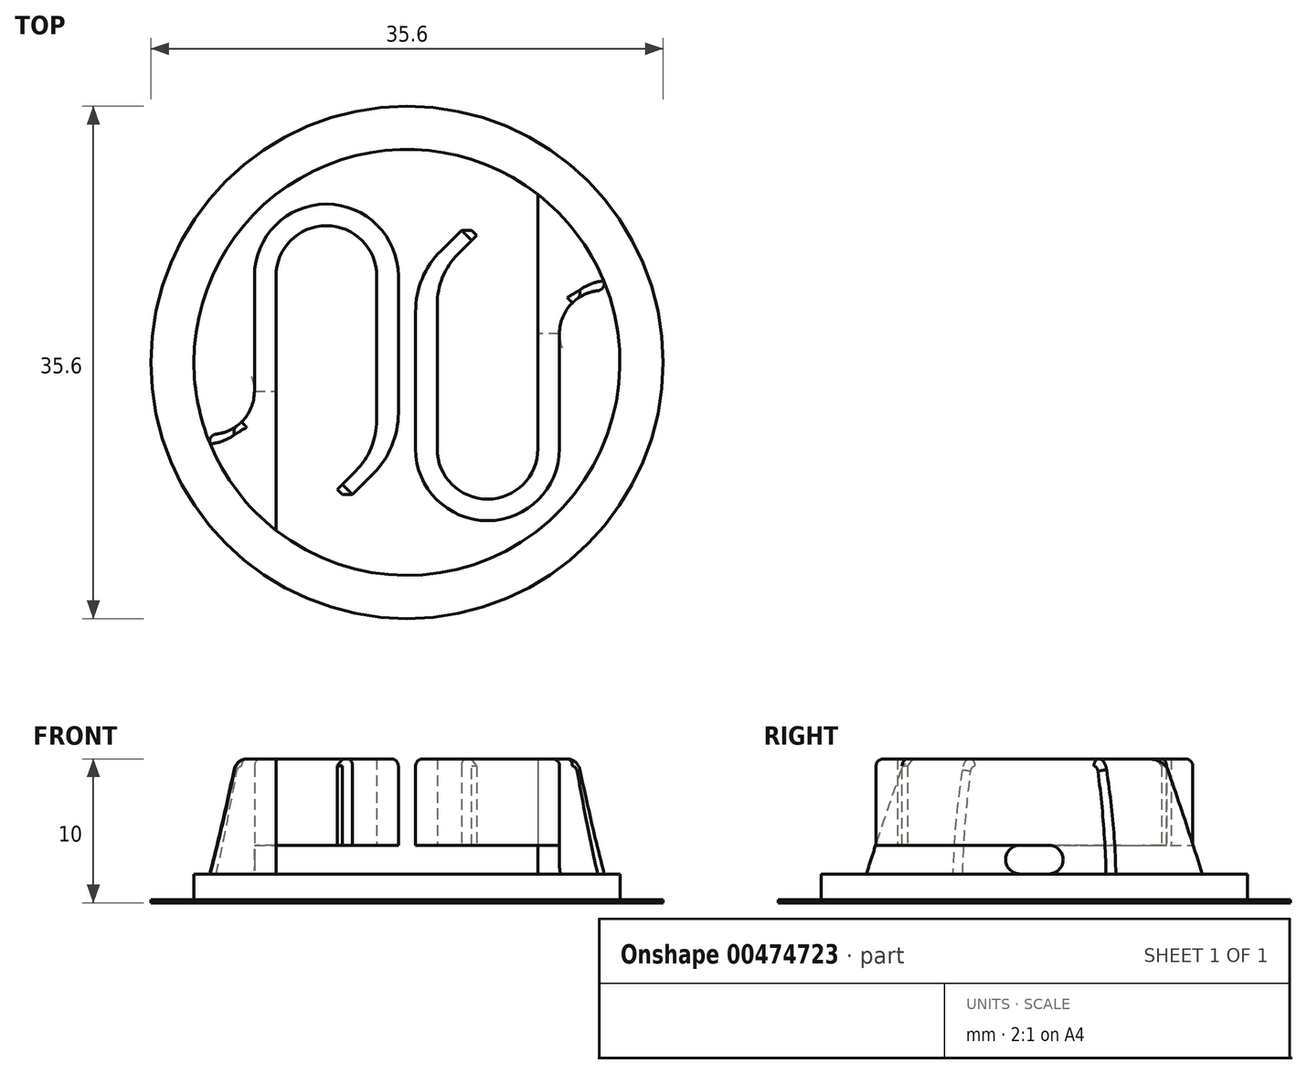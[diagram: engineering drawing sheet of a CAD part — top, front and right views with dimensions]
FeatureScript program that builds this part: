
annotation { "Feature Type Name" : "Feature", "Feature Type Description" : "" }
export const myFeature = defineFeature(function(context is Context, id is Id, definition is map)
    precondition{}
    {
        {
            var Q0;
            Q0=qCreatedBy(makeId("Top.planeOp"),FACE);
            var sketch = newSketch(context, id + "F0", { "sketchPlane" : qUnion([Q0])});
            skCircle(sketch, "E0", {"center": v(0, 0) * mm, "radius": 14.8 * mm});
            skSolve(sketch);
        }
        {
            var Q0;
            Q0=qSketchRegion(id+"F0",true);
            extrude(context, id + "F1", {"entities" : qUnion([Q0]), "depth" : 2 * mm, "offsetDistance" : 25 * mm});
        }
        {
            var Q0;
            Q0=makeQuery(id+"F1.opExtrude","CAP_FACE",FACE,{"disambiguationData":[OSD([sQuery(id+"F0.wireOp",EDGE,"E0")])],"isStart":false});
            var sketch = newSketch(context, id + "F2", { "sketchPlane" : qUnion([Q0])});
            skLineSegment(sketch, "E1.bottom", {"start": v(-0.75, 9.5) * mm, "end": v(0.75, 9.5) * mm, "construction": true});
            skLineSegment(sketch, "E1.top", {"start": v(-0.75, -9.5) * mm, "end": v(0.75, -9.5) * mm, "construction": true});
            skLineSegment(sketch, "E1.left", {"start": v(-0.75, 9.5) * mm, "end": v(-0.75, -9.5) * mm, "construction": true});
            skLineSegment(sketch, "E1.right", {"start": v(0.75, 9.5) * mm, "end": v(0.75, -9.5) * mm, "construction": true});
            skLineSegment(sketch, "E2", {"start": v(-12.82, -7.4) * mm, "end": v(12.82, 7.4) * mm, "construction": true});
            skLineSegment(sketch, "E3", {"start": v(-0.6, 6) * mm, "end": v(-0.6, -3.51) * mm});
            skLineSegment(sketch, "E4", {"start": v(-2.36, -7.76) * mm, "end": v(-4.14, -9.54) * mm});
            skLineSegment(sketch, "E5", {"start": v(-4.14, -9.54) * mm, "end": v(-4.84, -8.83) * mm});
            skLineSegment(sketch, "E6", {"start": v(-4.84, -8.83) * mm, "end": v(-3.56, -7.55) * mm});
            skLineSegment(sketch, "E7", {"start": v(-2.1, -4.01) * mm, "end": v(-2.1, 6) * mm});
            skArc(sketch, "E8", {"start": v(-0.6, 6) * mm, "mid": v(-5.6, 11) * mm, "end": v(-10.6, 6) * mm});
            skLineSegment(sketch, "E9", {"start": v(-10.6, -2) * mm, "end": v(-10.6, 6) * mm});
            skLineSegment(sketch, "E10", {"start": v(-9.1, -11.67) * mm, "end": v(-9.1, 6) * mm});
            skArc(sketch, "E11", {"start": v(-2.1, 6) * mm, "mid": v(-5.6, 9.5) * mm, "end": v(-9.1, 6) * mm});
            skPoint(sketch, "E12.visualSharp", {"position": v(-2.1, -6.09) * mm});
            skArc(sketch, "E12.filletArc", {"start": v(-3.56, -7.55) * mm, "mid": v(-2.48, -5.93) * mm, "end": v(-2.1, -4.01) * mm});
            skPoint(sketch, "E13.visualSharp", {"position": v(-0.6, -6) * mm});
            skArc(sketch, "E13.filletArc", {"start": v(-2.36, -7.76) * mm, "mid": v(-1.06, -5.81) * mm, "end": v(-0.6, -3.51) * mm});
            skArc(sketch, "E14", {"start": v(-13.94, -4.98) * mm, "mid": v(-11.6, -4.24) * mm, "end": v(-10.6, -2) * mm});
            skArc(sketch, "E15", {"start": v(-13.94, -4.98) * mm, "mid": v(-12, -8.67) * mm, "end": v(-9.1, -11.67) * mm});
            skLineSegment(sketch, "E16", {"start": v(0.6, 3.51) * mm, "end": v(0.6, -6) * mm});
            skArc(sketch, "E17", {"start": v(0.6, -6) * mm, "mid": v(5.6, -11) * mm, "end": v(10.6, -6) * mm});
            skLineSegment(sketch, "E18", {"start": v(2.1, 4.01) * mm, "end": v(2.1, -6) * mm});
            skLineSegment(sketch, "E19", {"start": v(3.56, 7.55) * mm, "end": v(4.84, 8.83) * mm});
            skLineSegment(sketch, "E20", {"start": v(4.84, 8.83) * mm, "end": v(4.14, 9.54) * mm});
            skLineSegment(sketch, "E21", {"start": v(4.14, 9.54) * mm, "end": v(2.36, 7.76) * mm});
            skArc(sketch, "E22", {"start": v(2.1, -6) * mm, "mid": v(5.6, -9.5) * mm, "end": v(9.1, -6) * mm});
            skLineSegment(sketch, "E23", {"start": v(9.1, -6) * mm, "end": v(9.1, 11.67) * mm});
            skLineSegment(sketch, "E24", {"start": v(10.6, -6) * mm, "end": v(10.6, 2) * mm});
            skArc(sketch, "E25", {"start": v(13.94, 4.98) * mm, "mid": v(11.6, 4.24) * mm, "end": v(10.6, 2) * mm});
            skArc(sketch, "E26", {"start": v(13.94, 4.98) * mm, "mid": v(12, 8.67) * mm, "end": v(9.1, 11.67) * mm});
            skPoint(sketch, "E27.visualSharp", {"position": v(2.1, 6.09) * mm});
            skArc(sketch, "E27.filletArc", {"start": v(3.56, 7.55) * mm, "mid": v(2.48, 5.93) * mm, "end": v(2.1, 4.01) * mm});
            skPoint(sketch, "E28.visualSharp", {"position": v(0.6, 6) * mm});
            skArc(sketch, "E28.filletArc", {"start": v(2.36, 7.76) * mm, "mid": v(1.06, 5.81) * mm, "end": v(0.6, 3.51) * mm});
            skSolve(sketch);
        }
        {
            var Q0;
            Q0=qSketchRegion(id+"F2",true);
            extrude(context, id + "F3", {"entities" : qUnion([Q0]), "operationType" : NewBodyOperationType.ADD, "depth" : 8 * mm, "offsetDistance" : 25 * mm});
        }
        {
            var Q0;
            Q0=makeQuery(id+"F3.opExtrude","SWEPT_FACE",FACE,{"disambiguationData":[OSD([sQuery(id+"F2.wireOp",EDGE,"E16")])]});
            var sketch = newSketch(context, id + "F4", { "sketchPlane" : qUnion([Q0])});
            skLineSegment(sketch, "E29.bottom", {"start": v(-11.67, 2) * mm, "end": v(12.33, 2) * mm});
            skLineSegment(sketch, "E29.top", {"start": v(-11.67, 4) * mm, "end": v(12.33, 4) * mm});
            skLineSegment(sketch, "E29.left", {"start": v(-11.67, 2) * mm, "end": v(-11.67, 4) * mm});
            skLineSegment(sketch, "E29.right", {"start": v(12.33, 2) * mm, "end": v(12.33, 4) * mm});
            skSolve(sketch);
        }
        {
            var Q0;
            Q0=qSketchRegion(id+"F4",true);
            var Q1;
            Q1=makeQuery(id+"F3.opExtrude","SWEPT_FACE",FACE,{"disambiguationData":[OSD([sQuery(id+"F2.wireOp",EDGE,"E23")])]});
            extrude(context, id + "F5", {"entities" : qUnion([Q0]), "operationType" : NewBodyOperationType.REMOVE, "endBound" : BoundingType.UP_TO_SURFACE, "oppositeDirection" : true, "depth" : 25 * mm, "endBoundEntityFace" : qUnion([Q1]), "offsetDistance" : 25 * mm});
        }
        {
            var Q0;
            Q0=makeQuery(id+"F3.opExtrude","SWEPT_FACE",FACE,{"disambiguationData":[OSD([sQuery(id+"F2.wireOp",EDGE,"E24")])]});
            var sketch = newSketch(context, id + "F6", { "sketchPlane" : qUnion([Q0])});
            skLineSegment(sketch, "E30.bottom", {"start": v(-11.67, 4) * mm, "end": v(2, 4) * mm});
            skLineSegment(sketch, "E30.top", {"start": v(-11.67, 2) * mm, "end": v(2, 2) * mm});
            skLineSegment(sketch, "E30.left", {"start": v(-11.67, 4) * mm, "end": v(-11.67, 2) * mm});
            skLineSegment(sketch, "E30.right", {"start": v(2, 4) * mm, "end": v(2, 2) * mm});
            skSolve(sketch);
        }
        {
            var Q0;
            Q0=qSketchRegion(id+"F6",true);
            var Q1;
            {var subQ0=sQuery(id+"F2.wireOp",EDGE,"E23");Q1=makeQuery(id+"F5.boolean.opBoolean","MERGE",FACE,{"derivedFrom":[makeQuery(id+"F3.opExtrude","SWEPT_FACE",FACE,{"disambiguationData":[OSD([subQ0])]}),makeQuery(id+"F5.opExtrude","CAP_FACE",FACE,{"disambiguationData":[OSD([subQ0])],"isStart":false})]});}
            extrude(context, id + "F7", {"entities" : qUnion([Q0]), "operationType" : NewBodyOperationType.REMOVE, "endBound" : BoundingType.UP_TO_SURFACE, "oppositeDirection" : true, "depth" : 2 * mm, "endBoundEntityFace" : qUnion([Q1]), "offsetDistance" : 25 * mm});
        }
        {
            var Q0;
            Q0=makeQuery(id+"F3.opExtrude","SWEPT_FACE",FACE,{"disambiguationData":[OSD([sQuery(id+"F2.wireOp",EDGE,"E3")])]});
            var sketch = newSketch(context, id + "F8", { "sketchPlane" : qUnion([Q0])});
            skLineSegment(sketch, "E31.bottom", {"start": v(-11.67, 4) * mm, "end": v(12.33, 4) * mm});
            skLineSegment(sketch, "E31.top", {"start": v(-11.67, 2) * mm, "end": v(12.33, 2) * mm});
            skLineSegment(sketch, "E31.left", {"start": v(-11.67, 4) * mm, "end": v(-11.67, 2) * mm});
            skLineSegment(sketch, "E31.right", {"start": v(12.33, 4) * mm, "end": v(12.33, 2) * mm});
            skSolve(sketch);
        }
        {
            var Q0;
            Q0=qSketchRegion(id+"F8",true);
            var Q1;
            Q1=makeQuery(id+"F3.opExtrude","SWEPT_FACE",FACE,{"disambiguationData":[OSD([sQuery(id+"F2.wireOp",EDGE,"E10")])]});
            extrude(context, id + "F9", {"entities" : qUnion([Q0]), "operationType" : NewBodyOperationType.REMOVE, "endBound" : BoundingType.UP_TO_SURFACE, "oppositeDirection" : true, "depth" : 25 * mm, "endBoundEntityFace" : qUnion([Q1]), "offsetDistance" : 25 * mm});
        }
        {
            var Q0;
            Q0=makeQuery(id+"F3.opExtrude","SWEPT_FACE",FACE,{"disambiguationData":[OSD([sQuery(id+"F2.wireOp",EDGE,"E9")])]});
            var sketch = newSketch(context, id + "F10", { "sketchPlane" : qUnion([Q0])});
            skLineSegment(sketch, "E32.bottom", {"start": v(-11.67, 4) * mm, "end": v(2, 4) * mm});
            skLineSegment(sketch, "E32.top", {"start": v(-11.67, 2) * mm, "end": v(2, 2) * mm});
            skLineSegment(sketch, "E32.left", {"start": v(-11.67, 4) * mm, "end": v(-11.67, 2) * mm});
            skLineSegment(sketch, "E32.right", {"start": v(2, 4) * mm, "end": v(2, 2) * mm});
            skSolve(sketch);
        }
        {
            var Q0;
            Q0=qSketchRegion(id+"F10",true);
            var Q1;
            {var subQ0=sQuery(id+"F2.wireOp",EDGE,"E10");Q1=makeQuery(id+"F9.boolean.opBoolean","MERGE",FACE,{"derivedFrom":[makeQuery(id+"F3.opExtrude","SWEPT_FACE",FACE,{"disambiguationData":[OSD([subQ0])]}),makeQuery(id+"F9.opExtrude","CAP_FACE",FACE,{"disambiguationData":[OSD([subQ0])],"isStart":false})]});}
            extrude(context, id + "F11", {"entities" : qUnion([Q0]), "operationType" : NewBodyOperationType.REMOVE, "endBound" : BoundingType.UP_TO_SURFACE, "oppositeDirection" : true, "depth" : 25 * mm, "endBoundEntityFace" : qUnion([Q1]), "offsetDistance" : 25 * mm});
        }
        {
            var Q0;
            Q0=makeQuery(id+"F11.boolean.opBoolean","COPY",EDGE,{"derivedFrom":makeQuery(id+"F11.opExtrude","SWEPT_EDGE",EDGE,{"disambiguationData":[OSD([sQuery(id+"F2.wireOp",EDGE,"E9"),sQuery(id+"F2.wireOp",EDGE,"E14"),sQuery(id+"F10.wireOp",EDGE,"E32.bottom"),sQuery(id+"F10.wireOp",EDGE,"E32.right")])]})});
            var Q1;
            Q1=makeQuery(id+"F11.boolean.opBoolean","COPY",EDGE,{"derivedFrom":makeQuery(id+"F11.opExtrude","SWEPT_EDGE",EDGE,{"disambiguationData":[OSD([sQuery(id+"F10.wireOp",EDGE,"E32.top"),sQuery(id+"F10.wireOp",EDGE,"E32.right")])]})});
            var Q2;
            Q2=makeQuery(id+"F7.boolean.opBoolean","COPY",EDGE,{"derivedFrom":makeQuery(id+"F7.opExtrude","SWEPT_EDGE",EDGE,{"disambiguationData":[OSD([sQuery(id+"F6.wireOp",EDGE,"E30.top"),sQuery(id+"F6.wireOp",EDGE,"E30.right")])]})});
            var Q3;
            Q3=makeQuery(id+"F7.boolean.opBoolean","COPY",EDGE,{"derivedFrom":makeQuery(id+"F7.opExtrude","SWEPT_EDGE",EDGE,{"disambiguationData":[OSD([sQuery(id+"F2.wireOp",EDGE,"E24"),sQuery(id+"F2.wireOp",EDGE,"E25"),sQuery(id+"F6.wireOp",EDGE,"E30.bottom"),sQuery(id+"F6.wireOp",EDGE,"E30.right")])]})});
            var Q4;
            Q4=makeQuery(id+"F3.opExtrude","CAP_EDGE",EDGE,{"disambiguationData":[OSD([sQuery(id+"F2.wireOp",EDGE,"E25")])],"isStart":true});
            var Q5;
            {var subQ0=sQuery(id+"F4.wireOp",EDGE,"E29.bottom");var subQ1=sQuery(id+"F2.wireOp",EDGE,"E16");var subQ3=makeQuery(id+"F4.imprint","INTERSECT",VERTEX,{"derivedFrom":[makeQuery(id+"F3.opExtrude","SWEPT_EDGE",EDGE,{"disambiguationData":[OSD([subQ1,sQuery(id+"F2.wireOp",EDGE,"E28.filletArc")])]}),subQ0]});var subQ4=sQuery(id+"F2.wireOp",EDGE,"E23");Q5=makeQuery(id+"F5.boolean.opBoolean","MERGE",EDGE,{"derivedFrom":[makeQuery(id+"F3.opExtrude","CAP_EDGE",EDGE,{"disambiguationData":[OSD([subQ4])],"isStart":true}),makeQuery(id+"F5.opExtrude","TWEAK_EDGE",EDGE,{"derivedFrom":[makeQuery(id+"F3.opExtrude","SWEPT_FACE",FACE,{"disambiguationData":[OSD([subQ4])]}),makeQuery(id+"F4.imprint","IMPRINT",EDGE,{"disambiguationData":[TD([[makeQuery(id+"F4.imprint","INTERSECT",VERTEX,{"derivedFrom":[subQ0,sQuery(id+"F4.wireOp",EDGE,"E29.left")]}),-1.0]])],"derivedFrom":subQ0}),makeQuery(id+"F4.imprint","IMPRINT",EDGE,{"disambiguationData":[TD([[subQ3,-1.0]])],"derivedFrom":subQ0}),makeQuery(id+"F4.imprint","IMPRINT",EDGE,{"disambiguationData":[TD([[makeQuery(id+"F4.imprint","INTERSECT",VERTEX,{"derivedFrom":[subQ0,sQuery(id+"F4.wireOp",EDGE,"E29.right")]}),1.0]])],"derivedFrom":subQ0})]})]});}
            var Q6;
            Q6=makeQuery(id+"F3.opExtrude","CAP_EDGE",EDGE,{"disambiguationData":[OSD([sQuery(id+"F2.wireOp",EDGE,"E14")])],"isStart":true});
            var Q7;
            {var subQ0=sQuery(id+"F8.wireOp",EDGE,"E31.top");var subQ1=sQuery(id+"F2.wireOp",EDGE,"E3");var subQ2=makeQuery(id+"F8.imprint","INTERSECT",VERTEX,{"derivedFrom":[makeQuery(id+"F3.opExtrude","SWEPT_EDGE",EDGE,{"disambiguationData":[OSD([subQ1,sQuery(id+"F2.wireOp",EDGE,"E8")])]}),subQ0]});var subQ3=makeQuery(id+"F8.imprint","INTERSECT",VERTEX,{"derivedFrom":[makeQuery(id+"F3.opExtrude","SWEPT_EDGE",EDGE,{"disambiguationData":[OSD([subQ1,sQuery(id+"F2.wireOp",EDGE,"E13.filletArc")])]}),subQ0]});var subQ4=sQuery(id+"F2.wireOp",EDGE,"E10");Q7=makeQuery(id+"F9.boolean.opBoolean","MERGE",EDGE,{"derivedFrom":[makeQuery(id+"F3.opExtrude","CAP_EDGE",EDGE,{"disambiguationData":[OSD([subQ4])],"isStart":true}),makeQuery(id+"F9.opExtrude","TWEAK_EDGE",EDGE,{"derivedFrom":[makeQuery(id+"F3.opExtrude","SWEPT_FACE",FACE,{"disambiguationData":[OSD([subQ4])]}),makeQuery(id+"F8.imprint","IMPRINT",EDGE,{"disambiguationData":[TD([[subQ3,1.0],[makeQuery(id+"F8.imprint","INTERSECT",VERTEX,{"derivedFrom":[subQ0,sQuery(id+"F8.wireOp",EDGE,"E31.left")]}),-1.0]])],"derivedFrom":subQ0}),makeQuery(id+"F8.imprint","IMPRINT",EDGE,{"disambiguationData":[TD([[subQ2,-1.0],[subQ3,1.0]])],"derivedFrom":subQ0}),makeQuery(id+"F8.imprint","IMPRINT",EDGE,{"disambiguationData":[TD([[subQ2,-1.0],[makeQuery(id+"F8.imprint","INTERSECT",VERTEX,{"derivedFrom":[subQ0,sQuery(id+"F8.wireOp",EDGE,"E31.right")]}),1.0]])],"derivedFrom":subQ0})]})]});}
            fillet(context, id + "F12", {"entities" : qUnion([Q0, Q1, Q2, Q3, Q4, Q5, Q6, Q7]), "radius" : 1 * mm, "tangentPropagation" : true, "allowEdgeOverflow" : false});
        }
        {
            var Q0;
            Q0=makeQuery(id+"F3.opExtrude","CAP_EDGE",EDGE,{"disambiguationData":[OSD([sQuery(id+"F2.wireOp",EDGE,"E26")])],"isStart":false});
            var Q1;
            Q1=makeQuery(id+"F3.opExtrude","CAP_EDGE",EDGE,{"disambiguationData":[OSD([sQuery(id+"F2.wireOp",EDGE,"E15")])],"isStart":false});
            chamfer(context, id + "F13", {"entities" : qUnion([Q0, Q1]), "chamferType" : ChamferType.TWO_OFFSETS, "width1" : 2 * mm, "oppositeDirection" : false, "width2" : 8 * mm, "tangentPropagation" : true});
        }
        {
            var Q0;
            {var subQ0=sQuery(id+"F2.wireOp",EDGE,"E15");Q0=makeQuery(id+"F13.opChamfer","BLEND_EDGE",EDGE,{"blendedFrom":[makeQuery(id+"F3.opExtrude","CAP_EDGE",EDGE,{"disambiguationData":[OSD([subQ0])],"isStart":false}),makeQuery(id+"F3.opExtrude","CAP_FACE",FACE,{"disambiguationData":[OSD([sQuery(id+"F2.wireOp",EDGE,"E3"),sQuery(id+"F2.wireOp",EDGE,"E4"),sQuery(id+"F2.wireOp",EDGE,"E5"),sQuery(id+"F2.wireOp",EDGE,"E6"),sQuery(id+"F2.wireOp",EDGE,"E7"),sQuery(id+"F2.wireOp",EDGE,"E8"),sQuery(id+"F2.wireOp",EDGE,"E9"),sQuery(id+"F2.wireOp",EDGE,"E10"),sQuery(id+"F2.wireOp",EDGE,"E11"),sQuery(id+"F2.wireOp",EDGE,"E12.filletArc"),sQuery(id+"F2.wireOp",EDGE,"E13.filletArc"),sQuery(id+"F2.wireOp",EDGE,"E14"),subQ0])],"isStart":false})],"blendedInto":[makeQuery(id+"F3.opExtrude","CAP_FACE",FACE,{"disambiguationData":[OSD([sQuery(id+"F2.wireOp",EDGE,"E3"),sQuery(id+"F2.wireOp",EDGE,"E4"),sQuery(id+"F2.wireOp",EDGE,"E5"),sQuery(id+"F2.wireOp",EDGE,"E6"),sQuery(id+"F2.wireOp",EDGE,"E7"),sQuery(id+"F2.wireOp",EDGE,"E8"),sQuery(id+"F2.wireOp",EDGE,"E9"),sQuery(id+"F2.wireOp",EDGE,"E10"),sQuery(id+"F2.wireOp",EDGE,"E11"),sQuery(id+"F2.wireOp",EDGE,"E12.filletArc"),sQuery(id+"F2.wireOp",EDGE,"E13.filletArc"),sQuery(id+"F2.wireOp",EDGE,"E14"),subQ0])],"isStart":false})]});}
            var Q1;
            {var subQ0=sQuery(id+"F2.wireOp",EDGE,"E26");Q1=makeQuery(id+"F13.opChamfer","BLEND_EDGE",EDGE,{"blendedFrom":[makeQuery(id+"F3.opExtrude","CAP_EDGE",EDGE,{"disambiguationData":[OSD([subQ0])],"isStart":false}),makeQuery(id+"F3.opExtrude","CAP_FACE",FACE,{"disambiguationData":[OSD([sQuery(id+"F2.wireOp",EDGE,"E16"),sQuery(id+"F2.wireOp",EDGE,"E17"),sQuery(id+"F2.wireOp",EDGE,"E18"),sQuery(id+"F2.wireOp",EDGE,"E19"),sQuery(id+"F2.wireOp",EDGE,"E20"),sQuery(id+"F2.wireOp",EDGE,"E21"),sQuery(id+"F2.wireOp",EDGE,"E22"),sQuery(id+"F2.wireOp",EDGE,"E23"),sQuery(id+"F2.wireOp",EDGE,"E24"),sQuery(id+"F2.wireOp",EDGE,"E25"),subQ0,sQuery(id+"F2.wireOp",EDGE,"E27.filletArc"),sQuery(id+"F2.wireOp",EDGE,"E28.filletArc")])],"isStart":false})],"blendedInto":[makeQuery(id+"F3.opExtrude","CAP_FACE",FACE,{"disambiguationData":[OSD([sQuery(id+"F2.wireOp",EDGE,"E16"),sQuery(id+"F2.wireOp",EDGE,"E17"),sQuery(id+"F2.wireOp",EDGE,"E18"),sQuery(id+"F2.wireOp",EDGE,"E19"),sQuery(id+"F2.wireOp",EDGE,"E20"),sQuery(id+"F2.wireOp",EDGE,"E21"),sQuery(id+"F2.wireOp",EDGE,"E22"),sQuery(id+"F2.wireOp",EDGE,"E23"),sQuery(id+"F2.wireOp",EDGE,"E24"),sQuery(id+"F2.wireOp",EDGE,"E25"),subQ0,sQuery(id+"F2.wireOp",EDGE,"E27.filletArc"),sQuery(id+"F2.wireOp",EDGE,"E28.filletArc")])],"isStart":false})]});}
            fillet(context, id + "F14", {"entities" : qUnion([Q0, Q1]), "radius" : 1 * mm, "tangentPropagation" : true, "allowEdgeOverflow" : false});
        }
        {
            var Q0;
            Q0=makeQuery(id+"F3.opExtrude","CAP_EDGE",EDGE,{"disambiguationData":[OSD([sQuery(id+"F2.wireOp",EDGE,"E16")])],"isStart":false});
            var Q1;
            Q1=makeQuery(id+"F3.opExtrude","CAP_EDGE",EDGE,{"disambiguationData":[OSD([sQuery(id+"F2.wireOp",EDGE,"E3")])],"isStart":false});
            var Q2;
            Q2=makeQuery(id+"F5.boolean.opBoolean","COPY",EDGE,{"derivedFrom":makeQuery(id+"F5.opExtrude","CAP_EDGE",EDGE,{"disambiguationData":[OSD([sQuery(id+"F4.wireOp",EDGE,"E29.top")])],"isStart":true})});
            var Q3;
            Q3=makeQuery(id+"F9.boolean.opBoolean","COPY",EDGE,{"derivedFrom":makeQuery(id+"F9.opExtrude","CAP_EDGE",EDGE,{"disambiguationData":[OSD([sQuery(id+"F8.wireOp",EDGE,"E31.bottom")])],"isStart":true})});
            fillet(context, id + "F15", {"entities" : qUnion([Q0, Q1, Q2, Q3]), "radius" : 0.5 * mm, "tangentPropagation" : true, "allowEdgeOverflow" : false});
        }
        {
            var Q0;
            Q0=makeQuery(id+"F3.opExtrude","CAP_EDGE",EDGE,{"disambiguationData":[OSD([sQuery(id+"F2.wireOp",EDGE,"E20")])],"isStart":false});
            var Q1;
            Q1=makeQuery(id+"F3.opExtrude","CAP_EDGE",EDGE,{"disambiguationData":[OSD([sQuery(id+"F2.wireOp",EDGE,"E5")])],"isStart":false});
            chamfer(context, id + "F16", {"entities" : qUnion([Q0, Q1]), "width" : 0.5 * mm, "tangentPropagation" : true});
        }
        {
            var Q0;
            Q0=makeQuery(id+"F1.opExtrude","CAP_FACE",FACE,{"disambiguationData":[OSD([sQuery(id+"F0.wireOp",EDGE,"E0")])],"isStart":true});
            var sketch = newSketch(context, id + "F17", { "sketchPlane" : qUnion([Q0])});
            skCircle(sketch, "E33", {"center": v(0, 0) * mm, "radius": 17.8 * mm});
            skCircle(sketch, "E34", {"center": v(0, 0) * mm, "radius": 14.8 * mm});
            skSolve(sketch);
        }
        {
            var Q0;
            Q0 = qSketchRegion(id + "F17", true);
            extrude(context, id + "F18", {"entities" : qUnion([Q0]), "operationType" : NewBodyOperationType.ADD, "oppositeDirection" : true, "depth" : 0.2 * mm, "offsetDistance" : 25 * mm});
        }
    });
